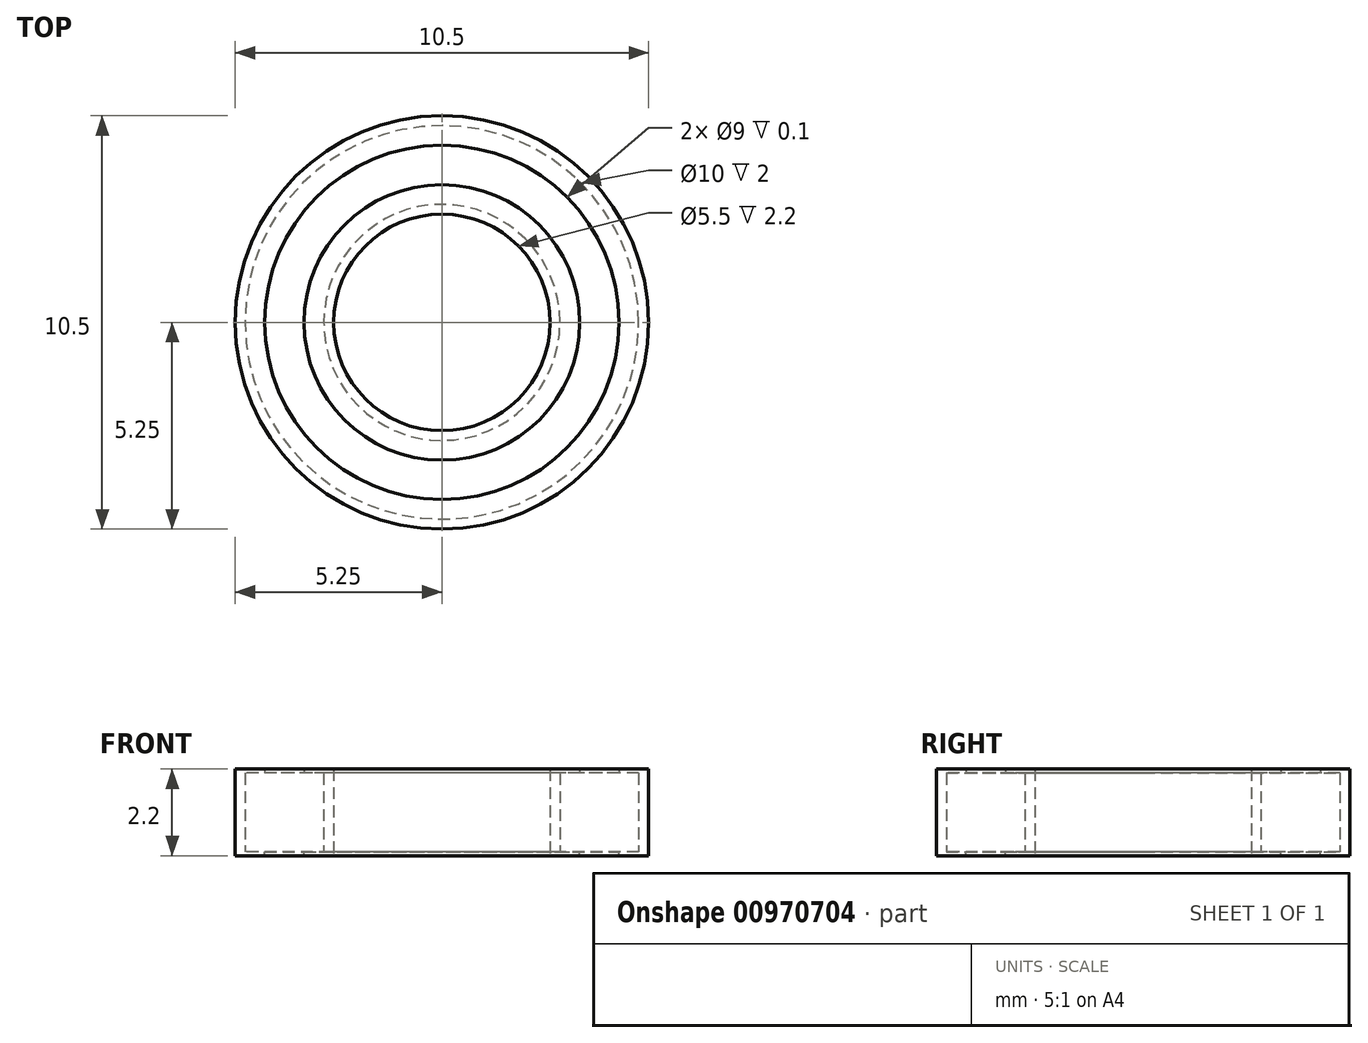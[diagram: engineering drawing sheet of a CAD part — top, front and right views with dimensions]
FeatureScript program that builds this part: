
annotation { "Feature Type Name" : "Feature", "Feature Type Description" : "" }
export const myFeature = defineFeature(function(context is Context, id is Id, definition is map)
    precondition{}
    {
        {
            var Q0;
            Q0=qCreatedBy(makeId("Top.planeOp"),FACE);
            var sketch = newSketch(context, id + "F0", { "sketchPlane" : qUnion([Q0])});
            skCircle(sketch, "E0", {"center": v(0, 0) * mm, "radius": 5 * mm});
            skCircle(sketch, "E1", {"center": v(0, 0) * mm, "radius": 3 * mm});
            skCircle(sketch, "E2", {"center": v(0, 0) * mm, "radius": 2.75 * mm});
            skCircle(sketch, "E3", {"center": v(0, 0) * mm, "radius": 5.25 * mm});
            skSolve(sketch);
        }
        {
            var Q0;
            Q0=makeQuery(id+"F0.imprint","IMPRINT",FACE,{"disambiguationData":[TD([[makeQuery(id+"F0.imprint","IMPRINT",EDGE,{"derivedFrom":sQuery(id+"F0.wireOp",EDGE,"E0")}),-1.0]])]});
            var Q1;
            Q1=makeQuery(id+"F0.imprint","IMPRINT",FACE,{"disambiguationData":[TD([[makeQuery(id+"F0.imprint","IMPRINT",EDGE,{"derivedFrom":sQuery(id+"F0.wireOp",EDGE,"E1")}),1.0]])]});
            extrude(context, id + "F1", {"entities" : qUnion([Q0, Q1]), "depth" : 2 * mm, "offsetDistance" : 25 * mm});
        }
        {
            var Q0;
            Q0=qCreatedBy(makeId("Right.planeOp"),FACE);
            var sketch = newSketch(context, id + "F2", { "sketchPlane" : qUnion([Q0])});
            skArc(sketch, "E4", {"start": v(-11.15, 1.73) * mm, "mid": v(-10.15, 0.73) * mm, "end": v(-9.15, 1.73) * mm});
            skLineSegment(sketch, "E5", {"start": v(-11.15, 1.73) * mm, "end": v(-9.15, 1.73) * mm, "construction": true});
            skSolve(sketch);
        }
        {
            var Q0;
            Q0=sQuery(id+"F2.wireOp",EDGE,"E4");
            var Q1;
            Q1=sQuery(id+"F2.wireOp",EDGE,"E5");
            revolve(context, id + "F3", {"bodyType" : ToolBodyType.SURFACE, "surfaceOperationType" : NewSurfaceOperationType.NEW, "surfaceEntities" : qUnion([Q0]), "axis" : qUnion([Q1]), "revolveType" : RevolveType.FULL});
        }
        {
            var Q0;
            Q0=makeQuery(id+"F3.opRevolve","SWEPT_BODY",BODY,{"disambiguationData":[OSD([sQuery(id+"F2.wireOp",EDGE,"E4")])]});
            transform(context, id + "F4", {"entities" : qUnion([Q0]), "transformType" : TransformType.TRANSLATION_3D, "dx" : 0 * mm, "dy" : 6.15 * mm, "dz" : 0 * mm, "makeCopy" : false});
        }
        {
            var Q0;
            Q0=makeQuery(id+"F3.opRevolve","SWEPT_BODY",BODY,{"disambiguationData":[OSD([sQuery(id+"F2.wireOp",EDGE,"E4")])]});
            var Q1;
            Q1=makeQuery(id+"F1.opExtrude","CAP_EDGE",EDGE,{"disambiguationData":[OSD([sQuery(id+"F0.wireOp",EDGE,"E1")])],"isStart":false});
            circularPattern(context, id + "F5", {"entities" : qUnion([Q0]), "axis" : qUnion([Q1]), "angle" : 360 * degree, "instanceCount" : 10, "equalSpace" : true});
        }
        {
            var Q0;
            Q0=makeQuery(id+"F5.opPattern","COPY",BODY,{"derivedFrom":makeQuery(id+"F3.opRevolve","SWEPT_BODY",BODY,{"disambiguationData":[OSD([sQuery(id+"F2.wireOp",EDGE,"E4")])]}),"instanceName":"7"});
            var Q1;
            Q1=makeQuery(id+"F5.opPattern","COPY",BODY,{"derivedFrom":makeQuery(id+"F3.opRevolve","SWEPT_BODY",BODY,{"disambiguationData":[OSD([sQuery(id+"F2.wireOp",EDGE,"E4")])]}),"instanceName":"6"});
            var Q2;
            Q2=makeQuery(id+"F5.opPattern","COPY",BODY,{"derivedFrom":makeQuery(id+"F3.opRevolve","SWEPT_BODY",BODY,{"disambiguationData":[OSD([sQuery(id+"F2.wireOp",EDGE,"E4")])]}),"instanceName":"5"});
            var Q3;
            Q3=makeQuery(id+"F5.opPattern","COPY",BODY,{"derivedFrom":makeQuery(id+"F3.opRevolve","SWEPT_BODY",BODY,{"disambiguationData":[OSD([sQuery(id+"F2.wireOp",EDGE,"E4")])]}),"instanceName":"4"});
            var Q4;
            Q4=makeQuery(id+"F5.opPattern","COPY",BODY,{"derivedFrom":makeQuery(id+"F3.opRevolve","SWEPT_BODY",BODY,{"disambiguationData":[OSD([sQuery(id+"F2.wireOp",EDGE,"E4")])]}),"instanceName":"3"});
            var Q5;
            Q5=makeQuery(id+"F5.opPattern","COPY",BODY,{"derivedFrom":makeQuery(id+"F3.opRevolve","SWEPT_BODY",BODY,{"disambiguationData":[OSD([sQuery(id+"F2.wireOp",EDGE,"E4")])]}),"instanceName":"2"});
            var Q6;
            Q6=makeQuery(id+"F5.opPattern","COPY",BODY,{"derivedFrom":makeQuery(id+"F3.opRevolve","SWEPT_BODY",BODY,{"disambiguationData":[OSD([sQuery(id+"F2.wireOp",EDGE,"E4")])]}),"instanceName":"1"});
            var Q7;
            Q7=makeQuery(id+"F3.opRevolve","SWEPT_BODY",BODY,{"disambiguationData":[OSD([sQuery(id+"F2.wireOp",EDGE,"E4")])]});
            var Q8;
            Q8=makeQuery(id+"F5.opPattern","COPY",BODY,{"derivedFrom":makeQuery(id+"F3.opRevolve","SWEPT_BODY",BODY,{"disambiguationData":[OSD([sQuery(id+"F2.wireOp",EDGE,"E4")])]}),"instanceName":"9"});
            var Q9;
            Q9=makeQuery(id+"F5.opPattern","COPY",BODY,{"derivedFrom":makeQuery(id+"F3.opRevolve","SWEPT_BODY",BODY,{"disambiguationData":[OSD([sQuery(id+"F2.wireOp",EDGE,"E4")])]}),"instanceName":"8"});
            transform(context, id + "F6", {"entities" : qUnion([Q0, Q1, Q2, Q3, Q4, Q5, Q6, Q7, Q8, Q9]), "transformType" : TransformType.TRANSLATION_3D, "dx" : 0 * mm, "dy" : 0 * mm, "dz" : -0.75 * mm, "makeCopy" : false});
        }
        {
            var Q0;
            Q0=makeQuery(id+"F1.opExtrude","CAP_FACE",FACE,{"disambiguationData":[OSD([sQuery(id+"F0.wireOp",EDGE,"E1"),sQuery(id+"F0.wireOp",EDGE,"E2")])],"isStart":false});
            var sketch = newSketch(context, id + "F7", { "sketchPlane" : qUnion([Q0])});
            skCircle(sketch, "E6.0", {"center": v(0, 0) * mm, "radius": 5 * mm});
            skCircle(sketch, "E7.0", {"center": v(0, 0) * mm, "radius": 5.25 * mm});
            skCircle(sketch, "E8.0", {"center": v(0, 0) * mm, "radius": 3 * mm});
            skCircle(sketch, "E9.0", {"center": v(0, 0) * mm, "radius": 2.75 * mm});
            skCircle(sketch, "E10", {"center": v(0, 0) * mm, "radius": 3.5 * mm});
            skCircle(sketch, "E11", {"center": v(0, 0) * mm, "radius": 4.5 * mm});
            skSolve(sketch);
        }
        {
            var Q0;
            Q0=makeQuery(id+"F7.imprint","IMPRINT",FACE,{"disambiguationData":[TD([[makeQuery(id+"F7.imprint","IMPRINT",EDGE,{"derivedFrom":sQuery(id+"F7.wireOp",EDGE,"E6.0")}),1.0]])]});
            var Q1;
            Q1=makeQuery(id+"F7.imprint","IMPRINT",FACE,{"disambiguationData":[TD([[makeQuery(id+"F7.imprint","IMPRINT",EDGE,{"derivedFrom":sQuery(id+"F7.wireOp",EDGE,"E6.0")}),-1.0]])]});
            var Q2;
            Q2=makeQuery(id+"F7.imprint","IMPRINT",FACE,{"disambiguationData":[TD([[makeQuery(id+"F7.imprint","IMPRINT",EDGE,{"derivedFrom":sQuery(id+"F7.wireOp",EDGE,"E8.0")}),-1.0]])]});
            var Q3;
            Q3=makeQuery(id+"F7.imprint","IMPRINT",FACE,{"disambiguationData":[TD([[makeQuery(id+"F7.imprint","IMPRINT",EDGE,{"derivedFrom":sQuery(id+"F7.wireOp",EDGE,"E8.0")}),1.0]])]});
            extrude(context, id + "F8", {"entities" : qUnion([Q0, Q1, Q2, Q3]), "operationType" : NewBodyOperationType.ADD, "depth" : 0.1 * mm, "offsetDistance" : 25 * mm});
        }
        {
            var Q0;
            Q0=makeQuery(id+"F1.opExtrude","CAP_FACE",FACE,{"disambiguationData":[OSD([sQuery(id+"F0.wireOp",EDGE,"E1"),sQuery(id+"F0.wireOp",EDGE,"E2")])],"isStart":true});
            var sketch = newSketch(context, id + "F9", { "sketchPlane" : qUnion([Q0])});
            skCircle(sketch, "E12", {"center": v(0, 0) * mm, "radius": 3.5 * mm});
            skCircle(sketch, "E13", {"center": v(0, 0) * mm, "radius": 4.5 * mm});
            skCircle(sketch, "E14.0", {"center": v(0, 0) * mm, "radius": 5.25 * mm});
            skSolve(sketch);
        }
        {
            var Q0;
            Q0=makeQuery(id+"F9.imprint","IMPRINT",FACE,{"disambiguationData":[TD([[makeQuery(id+"F9.imprint","IMPRINT",EDGE,{"derivedFrom":sQuery(id+"F9.wireOp",EDGE,"E12")}),1.0]])]});
            var Q1;
            Q1=makeQuery(id+"F9.imprint","IMPRINT",FACE,{"disambiguationData":[TD([[makeQuery(id+"F9.imprint","IMPRINT",EDGE,{"derivedFrom":makeQuery(id+"F1.opExtrude","CAP_EDGE",EDGE,{"disambiguationData":[OSD([sQuery(id+"F0.wireOp",EDGE,"E1")])],"isStart":true})}),-1.0]])]});
            var Q2;
            Q2=makeQuery(id+"F9.imprint","IMPRINT",FACE,{"disambiguationData":[TD([[makeQuery(id+"F9.imprint","IMPRINT",EDGE,{"derivedFrom":sQuery(id+"F9.wireOp",EDGE,"E13")}),-1.0]])]});
            extrude(context, id + "F10", {"entities" : qUnion([Q0, Q1, Q2]), "operationType" : NewBodyOperationType.ADD, "depth" : 0.1 * mm, "offsetDistance" : 25 * mm});
        }
    });
